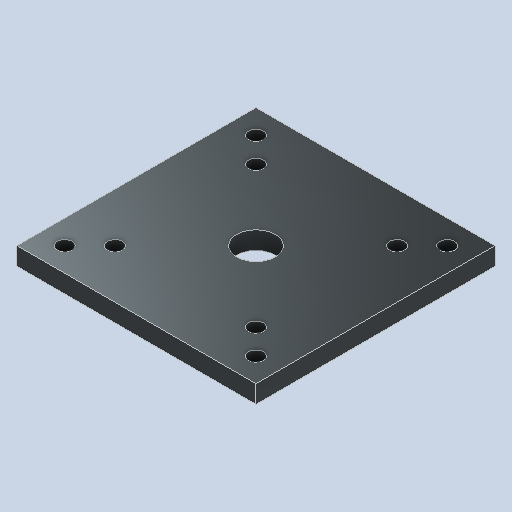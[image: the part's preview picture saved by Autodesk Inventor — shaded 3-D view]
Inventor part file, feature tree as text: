
AUTODESK INVENTOR PART (.ipt)
format: ipt  version: 2023 (Build 270158000, 158)  size: 272,384 bytes
history: native  units: mm
features: sketch x4, hole x3, other x1, extrude x1
ambient origin geometry x8: Origin, YZ Plane, XZ Plane, XY Plane, X Axis, Y Axis, Z Axis, Center Point
bodies: Body1 (feature_tree)
feature tree (9):
  other  "Sólido1"
  extrude  "Extrusão1"  Depth=80.0mm
  hole  "Furo1"  [1 undecoded]
  hole  "Furo2"  [1 undecoded]
  hole  "Furo3"  [1 undecoded]
  sketch  "Esboço1"  dims[d0=80.0mm d1=80.0mm]
  sketch  "Esboço2"  dims[d2=6.0mm d3=0.0mm d4=47.2mm]
  sketch  "Esboço3"  dims[d5=47.2mm d6=47.2mm]
  sketch  "Esboço4"  dims[d7=47.2mm d8=0.0mm d9=0.0mm d10=80.0mm d11=16.4mm d12=16.4mm d13=5.0mm d14=6.0mm d15=4.0mm d16=2.0mm d17=90.0deg d18=0.5mm d19=20.594885mm d20=8.0mm d21=8.0mm d22=8.0mm d23=8.0mm d24=8.0mm d25=8.0mm d26=8.0mm d27=8.0mm d28=5.0mm d29=6.0mm d30=4.0mm d31=2.0mm d32=90.0deg d33=8.0mm d34=20.594885mm d35=80.0mm d36=40.0mm d37=40.0mm d38=13.0mm d39=6.0mm d40=4.0mm d41=2.0mm d42=90.0deg d43=8.0mm d44=20.594885mm]
note: 3 required parameter values undecoded (feature->parameter linkage not recoverable at this tier; creation-order binding heuristic only, values carry confidence <= 0.55)
